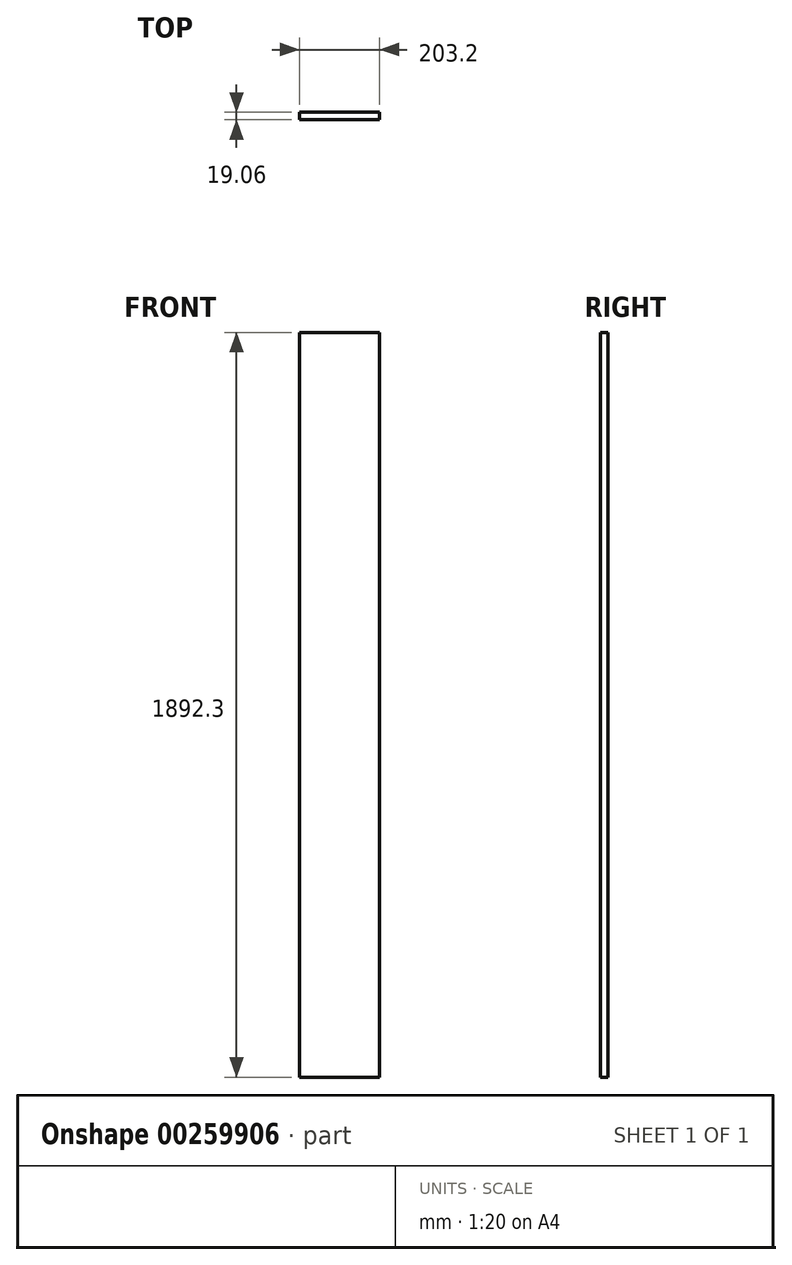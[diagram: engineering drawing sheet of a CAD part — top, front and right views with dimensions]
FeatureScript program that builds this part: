
annotation { "Feature Type Name" : "Feature", "Feature Type Description" : "" }
export const myFeature = defineFeature(function(context is Context, id is Id, definition is map)
    precondition{}
    {
        {
            var Q0;
            Q0=qCreatedBy(makeId("Top.planeOp"),FACE);
            var sketch = newSketch(context, id + "F0", { "sketchPlane" : qUnion([Q0])});
            skLineSegment(sketch, "E0.bottom", {"start": v(-101.6, 9.53) * mm, "end": v(101.6, 9.53) * mm});
            skLineSegment(sketch, "E0.top", {"start": v(-101.6, -9.53) * mm, "end": v(101.6, -9.53) * mm});
            skLineSegment(sketch, "E0.left", {"start": v(-101.6, 9.52) * mm, "end": v(-101.6, -9.53) * mm});
            skLineSegment(sketch, "E0.right", {"start": v(101.6, 9.53) * mm, "end": v(101.6, -9.52) * mm});
            skSolve(sketch);
        }
        {
            var Q0;
            Q0=makeQuery(id+"F0.imprint","IMPRINT",FACE,{"disambiguationData":[TD([[makeQuery(id+"F0.imprint","IMPRINT",EDGE,{"derivedFrom":sQuery(id+"F0.wireOp",EDGE,"E0.bottom")}),-1.0]])]});
            extrude(context, id + "F1", {"entities" : qUnion([Q0]), "endBound" : BoundingType.SYMMETRIC, "depth" : 1892.3 * mm});
        }
    });
